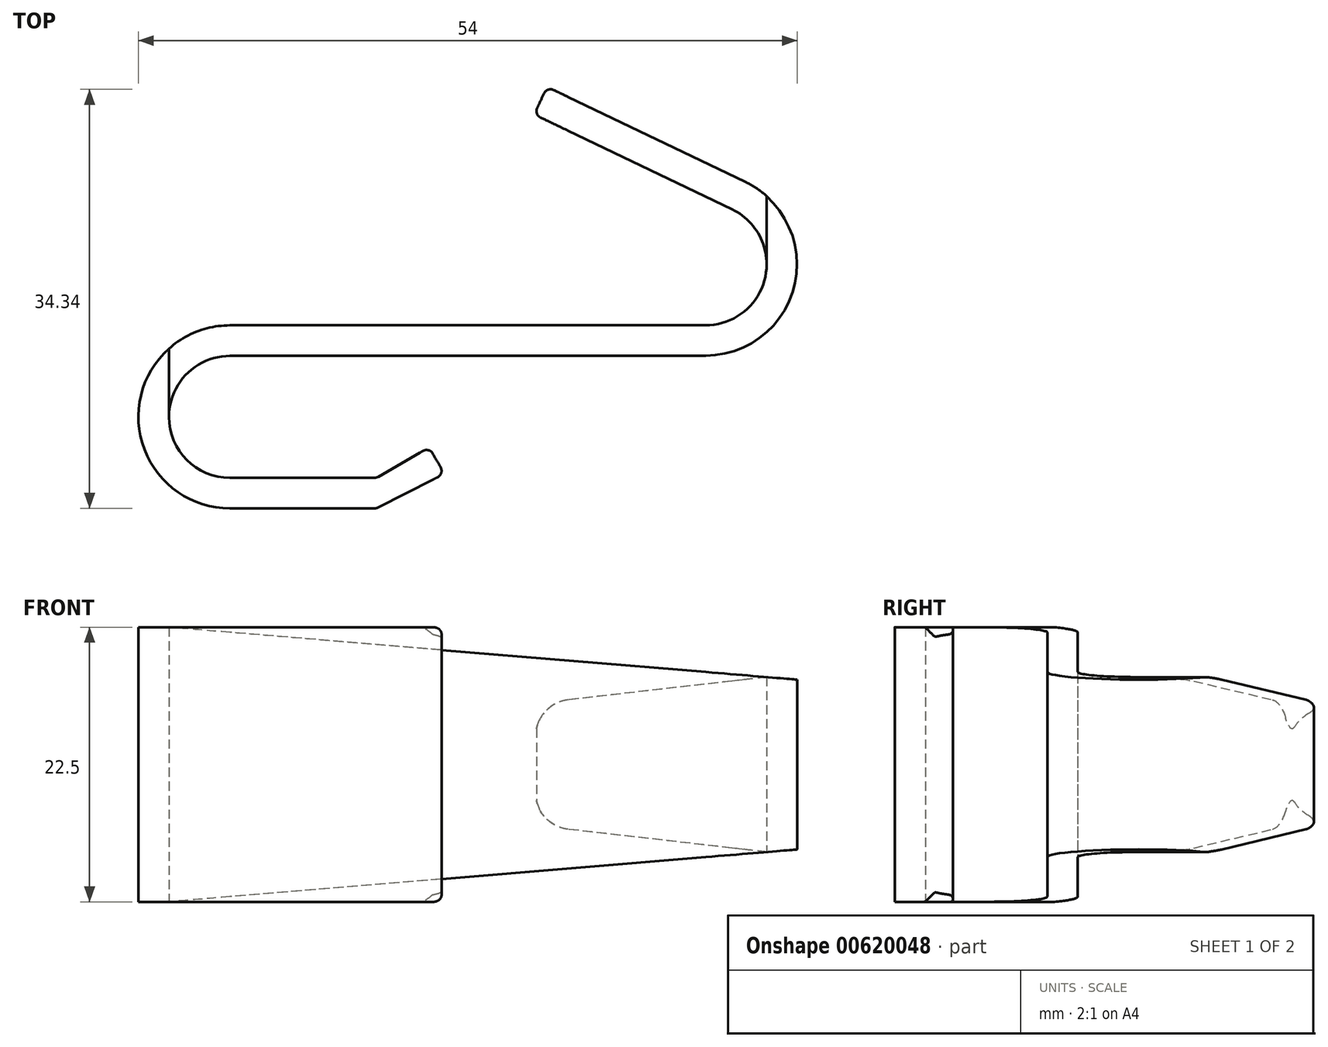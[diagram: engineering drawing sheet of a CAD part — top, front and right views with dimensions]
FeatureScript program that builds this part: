
annotation { "Feature Type Name" : "Feature", "Feature Type Description" : "" }
export const myFeature = defineFeature(function(context is Context, id is Id, definition is map)
    precondition{}
    {
        {
            var Q0;
            Q0=qCreatedBy(makeId("Top.planeOp"),FACE);
            var sketch = newSketch(context, id + "F0", { "sketchPlane" : qUnion([Q0])});
            skLineSegment(sketch, "E0", {"start": v(0, 0) * mm, "end": v(22, 0) * mm});
            skLineSegment(sketch, "E1", {"start": v(0, 0) * mm, "end": v(-22, 0) * mm});
            skLineSegment(sketch, "E2", {"start": v(22, 0) * mm, "end": v(17, 0) * mm, "construction": true});
            skLineSegment(sketch, "E3", {"start": v(-22, 0) * mm, "end": v(-22, -5) * mm, "construction": true});
            skArc(sketch, "E4", {"start": v(-22, 0) * mm, "mid": v(-27, -5) * mm, "end": v(-22, -10) * mm});
            skLineSegment(sketch, "E5", {"start": v(-22, -5) * mm, "end": v(-22, -10) * mm, "construction": true});
            skLineSegment(sketch, "E6", {"start": v(-22, -10) * mm, "end": v(-10.16, -10) * mm});
            skLineSegment(sketch, "E7", {"start": v(-10, -10) * mm, "end": v(11.67, -10) * mm, "construction": true});
            skLineSegment(sketch, "E8", {"start": v(-9.86, -9.92) * mm, "end": v(-6.18, -7.8) * mm});
            skLineSegment(sketch, "E9", {"start": v(-5.37, -8.01) * mm, "end": v(-4.73, -9.12) * mm});
            skLineSegment(sketch, "E10", {"start": v(-9.87, -12.44) * mm, "end": v(-4.98, -9.95) * mm});
            skLineSegment(sketch, "E11", {"start": v(-22, -12.5) * mm, "end": v(-10.14, -12.5) * mm});
            skArc(sketch, "E12", {"start": v(-22, 2.5) * mm, "mid": v(-29.5, -5) * mm, "end": v(-22, -12.5) * mm});
            skLineSegment(sketch, "E13", {"start": v(17, 2.5) * mm, "end": v(-22, 2.5) * mm});
            skLineSegment(sketch, "E14", {"start": v(17, 2.5) * mm, "end": v(17, 7.5) * mm, "construction": true});
            skArc(sketch, "E15", {"start": v(17, 2.5) * mm, "mid": v(21.88, 6.4) * mm, "end": v(19.16, 12) * mm});
            skArc(sketch, "E16", {"start": v(17, 0) * mm, "mid": v(24.31, 5.84) * mm, "end": v(20.24, 14.26) * mm});
            skLineSegment(sketch, "E17", {"start": v(20.24, 14.26) * mm, "end": v(4.55, 21.79) * mm});
            skLineSegment(sketch, "E18", {"start": v(19.16, 12) * mm, "end": v(3.47, 19.53) * mm});
            skLineSegment(sketch, "E19", {"start": v(3.75, 21.5) * mm, "end": v(3.19, 20.32) * mm});
            skPoint(sketch, "E20.visualSharp", {"position": v(-5.67, -7.5) * mm});
            skArc(sketch, "E20.filletArc", {"start": v(-5.37, -8.01) * mm, "mid": v(-5.73, -7.74) * mm, "end": v(-6.18, -7.8) * mm});
            skPoint(sketch, "E21.visualSharp", {"position": v(-4.42, -9.67) * mm});
            skArc(sketch, "E21.filletArc", {"start": v(-4.98, -9.95) * mm, "mid": v(-4.68, -9.59) * mm, "end": v(-4.73, -9.12) * mm});
            skPoint(sketch, "E22.visualSharp", {"position": v(-10, -12.5) * mm});
            skArc(sketch, "E22.filletArc", {"start": v(-10.14, -12.5) * mm, "mid": v(-10, -12.48) * mm, "end": v(-9.87, -12.44) * mm});
            skPoint(sketch, "E23.visualSharp", {"position": v(-10, -10) * mm});
            skArc(sketch, "E23.filletArc", {"start": v(-10.16, -10) * mm, "mid": v(-10, -9.98) * mm, "end": v(-9.86, -9.92) * mm});
            skPoint(sketch, "E24.visualSharp", {"position": v(2.93, 19.79) * mm});
            skArc(sketch, "E24.filletArc", {"start": v(3.19, 20.32) * mm, "mid": v(3.16, 19.87) * mm, "end": v(3.47, 19.53) * mm});
            skPoint(sketch, "E25.visualSharp", {"position": v(4, 22.04) * mm});
            skArc(sketch, "E25.filletArc", {"start": v(4.55, 21.79) * mm, "mid": v(4.1, 21.81) * mm, "end": v(3.75, 21.5) * mm});
            skSolve(sketch);
        }
        {
            var Q0;
            {var subQ0=sQuery(id+"F0.wireOp",EDGE,"E1");Q0=makeQuery(id+"F0.imprint","IMPRINT",FACE,{"disambiguationData":[TD([[makeQuery(id+"F0.imprint","IMPRINT",EDGE,{"derivedFrom":subQ0}),-1.0]])]});}
            extrude(context, id + "F1", {"entities" : qUnion([Q0]), "depth" : 11.25 * mm, "offsetDistance" : 25 * mm});
        }
        {
            var Q0;
            Q0=qCreatedBy(makeId("Front.planeOp"),FACE);
            cPlane(context, id + "F2", {"entities" : qUnion([Q0]), "cplaneType" : CPlaneType.OFFSET, "offset" : 5 * mm, "width" : 150 * mm, "height" : 150 * mm});
        }
        {
            var Q0;
            Q0=qCreatedBy(id+"F2.planeOp",FACE);
            var sketch = newSketch(context, id + "F3", { "sketchPlane" : qUnion([Q0])});
            skLineSegment(sketch, "E26", {"start": v(27, 15.76) * mm, "end": v(-27, 11.25) * mm});
            skLineSegment(sketch, "E27.0", {"start": v(27, 15.76) * mm, "end": v(27, 6.75) * mm});
            skLineSegment(sketch, "E28", {"start": v(27, 6.75) * mm, "end": v(-27, 11.25) * mm});
            skSolve(sketch);
        }
        {
            var Q0;
            Q0 = qSketchRegion(id + "F3", true);
            extrude(context, id + "F4", {"entities" : qUnion([Q0]), "operationType" : NewBodyOperationType.REMOVE, "oppositeDirection" : true, "depth" : 12.5 * mm, "offsetDistance" : 25 * mm});
        }
        {
            var Q0;
            Q0=qCreatedBy(makeId("Front.planeOp"),FACE);
            cPlane(context, id + "F5", {"entities" : qUnion([Q0]), "cplaneType" : CPlaneType.OFFSET, "offset" : 7.5 * mm, "oppositeDirection" : true, "width" : 150 * mm, "height" : 150 * mm});
        }
        {
            var Q0;
            Q0=qCreatedBy(id+"F5.planeOp",FACE);
            var sketch = newSketch(context, id + "F6", { "sketchPlane" : qUnion([Q0])});
            skPoint(sketch, "E29", {"position": v(24.5, 6.96) * mm});
            skPoint(sketch, "E30.end.orphan", {"position": v(22, 7.17) * mm});
            skLineSegment(sketch, "E31", {"start": v(3.06, 0) * mm, "end": v(3.06, 2.32) * mm, "construction": true});
            skLineSegment(sketch, "E32", {"start": v(24.5, 6.96) * mm, "end": v(22, 7.17) * mm});
            skLineSegment(sketch, "E33", {"start": v(22, 7.17) * mm, "end": v(5.72, 5.3) * mm});
            skLineSegment(sketch, "E34", {"start": v(3.06, 5) * mm, "end": v(1.37, 12.4) * mm});
            skLineSegment(sketch, "E35", {"start": v(1.37, 12.4) * mm, "end": v(25.52, 14.07) * mm});
            skLineSegment(sketch, "E36", {"start": v(25.52, 14.07) * mm, "end": v(24.5, 6.96) * mm});
            skPoint(sketch, "E37.visualSharp", {"position": v(3.06, 5) * mm});
            skArc(sketch, "E37.filletArc", {"start": v(5.72, 5.3) * mm, "mid": v(3.83, 4.32) * mm, "end": v(3.06, 2.32) * mm});
            skLineSegment(sketch, "E38", {"start": v(3.06, 5) * mm, "end": v(3.06, 2.32) * mm});
            skSolve(sketch);
        }
        {
            var Q0;
            Q0=makeQuery(id+"F1.opExtrude","SWEPT_FACE",FACE,{"disambiguationData":[OSD([sQuery(id+"F0.wireOp",EDGE,"E10")])]});
            var sketch = newSketch(context, id + "F7", { "sketchPlane" : qUnion([Q0])});
            skPoint(sketch, "E39", {"position": v(-14.43, 11.25) * mm});
            skPoint(sketch, "E40", {"position": v(-8.95, 11.25) * mm});
            skLineSegment(sketch, "E41", {"start": v(-10.37, 11.25) * mm, "end": v(-9.33, 11.25) * mm});
            skLineSegment(sketch, "E42", {"start": v(-8.33, 10.25) * mm, "end": v(-8.33, 10.17) * mm});
            skLineSegment(sketch, "E43", {"start": v(-8.33, 10.17) * mm, "end": v(-7.3, 10.17) * mm});
            skLineSegment(sketch, "E44", {"start": v(-7.3, 10.17) * mm, "end": v(-7.3, 12.2) * mm});
            skLineSegment(sketch, "E45", {"start": v(-7.3, 12.2) * mm, "end": v(-10.37, 11.25) * mm});
            skPoint(sketch, "E46.visualSharp", {"position": v(-8.33, 11.25) * mm});
            skArc(sketch, "E46.filletArc", {"start": v(-8.33, 10.25) * mm, "mid": v(-8.62, 10.96) * mm, "end": v(-9.33, 11.25) * mm});
            skSolve(sketch);
        }
        {
            var Q0;
            Q0 = qSketchRegion(id + "F6", true);
            extrude(context, id + "F8", {"entities" : qUnion([Q0]), "operationType" : NewBodyOperationType.REMOVE, "oppositeDirection" : true, "depth" : 25 * mm, "offsetDistance" : 25 * mm});
        }
        {
            var Q0;
            {var subQ1=sQuery(id+"F7.wireOp",EDGE,"E41");Q0=makeQuery(id+"F7.imprint","IMPRINT",FACE,{"disambiguationData":[TD([[makeQuery(id+"F7.imprint","IMPRINT",EDGE,{"derivedFrom":subQ1}),1.0]])]});}
            extrude(context, id + "F9", {"entities" : qUnion([Q0]), "operationType" : NewBodyOperationType.REMOVE, "oppositeDirection" : true, "depth" : 5 * mm, "offsetDistance" : 25 * mm});
        }
        {
            var Q0;
            {var subQ6=sQuery(id+"F7.wireOp",EDGE,"E41");Q0=makeQuery(id+"F7.imprint","IMPRINT",FACE,{"disambiguationData":[TD([[makeQuery(id+"F7.imprint","IMPRINT",EDGE,{"derivedFrom":subQ6}),1.0]])]});}
            var Q1;
            {var subQ0=sQuery(id+"F7.wireOp",EDGE,"E46.filletArc");var subQ1=sQuery(id+"F0.wireOp",EDGE,"E10");var subQ2=makeQuery(id+"F1.opExtrude","CAP_EDGE",EDGE,{"disambiguationData":[OSD([subQ1])],"isStart":false});var subQ3=makeQuery(id+"F7.imprint","INTERSECT",VERTEX,{"derivedFrom":[subQ2,sQuery(id+"F7.wireOp",EDGE,"E41"),subQ0]});Q1=makeQuery(id+"F7.imprint","IMPRINT",FACE,{"disambiguationData":[TD([[makeQuery(id+"F7.imprint","IMPRINT",EDGE,{"disambiguationData":[TD([[subQ3,1.0]])],"derivedFrom":subQ0}),-1.0]])]});}
            extrude(context, id + "F10", {"entities" : qUnion([Q0, Q1]), "operationType" : NewBodyOperationType.REMOVE, "oppositeDirection" : true, "depth" : 5 * mm, "offsetDistance" : 25 * mm});
        }
        {
            var Q0;
            Q0=makeQuery(id+"F1.opExtrude","SWEPT_BODY",BODY,{"disambiguationData":[OSD([sQuery(id+"F0.wireOp",EDGE,"E0"),sQuery(id+"F0.wireOp",EDGE,"E1"),sQuery(id+"F0.wireOp",EDGE,"E4"),sQuery(id+"F0.wireOp",EDGE,"E6"),sQuery(id+"F0.wireOp",EDGE,"E8"),sQuery(id+"F0.wireOp",EDGE,"E9"),sQuery(id+"F0.wireOp",EDGE,"E10"),sQuery(id+"F0.wireOp",EDGE,"E11"),sQuery(id+"F0.wireOp",EDGE,"E12"),sQuery(id+"F0.wireOp",EDGE,"E13"),sQuery(id+"F0.wireOp",EDGE,"E15"),sQuery(id+"F0.wireOp",EDGE,"E16"),sQuery(id+"F0.wireOp",EDGE,"E17"),sQuery(id+"F0.wireOp",EDGE,"E18"),sQuery(id+"F0.wireOp",EDGE,"E19"),sQuery(id+"F0.wireOp",EDGE,"E20.filletArc"),sQuery(id+"F0.wireOp",EDGE,"E21.filletArc"),sQuery(id+"F0.wireOp",EDGE,"E22.filletArc"),sQuery(id+"F0.wireOp",EDGE,"E23.filletArc"),sQuery(id+"F0.wireOp",EDGE,"E24.filletArc"),sQuery(id+"F0.wireOp",EDGE,"E25.filletArc")])]});
            var Q1;
            Q1=qCreatedBy(makeId("Top.planeOp"),FACE);
            mirror(context, id + "F11", {"operationType" : NewBodyOperationType.ADD, "entities" : qUnion([Q0]), "mirrorPlane" : qUnion([Q1])});
        }
    });
